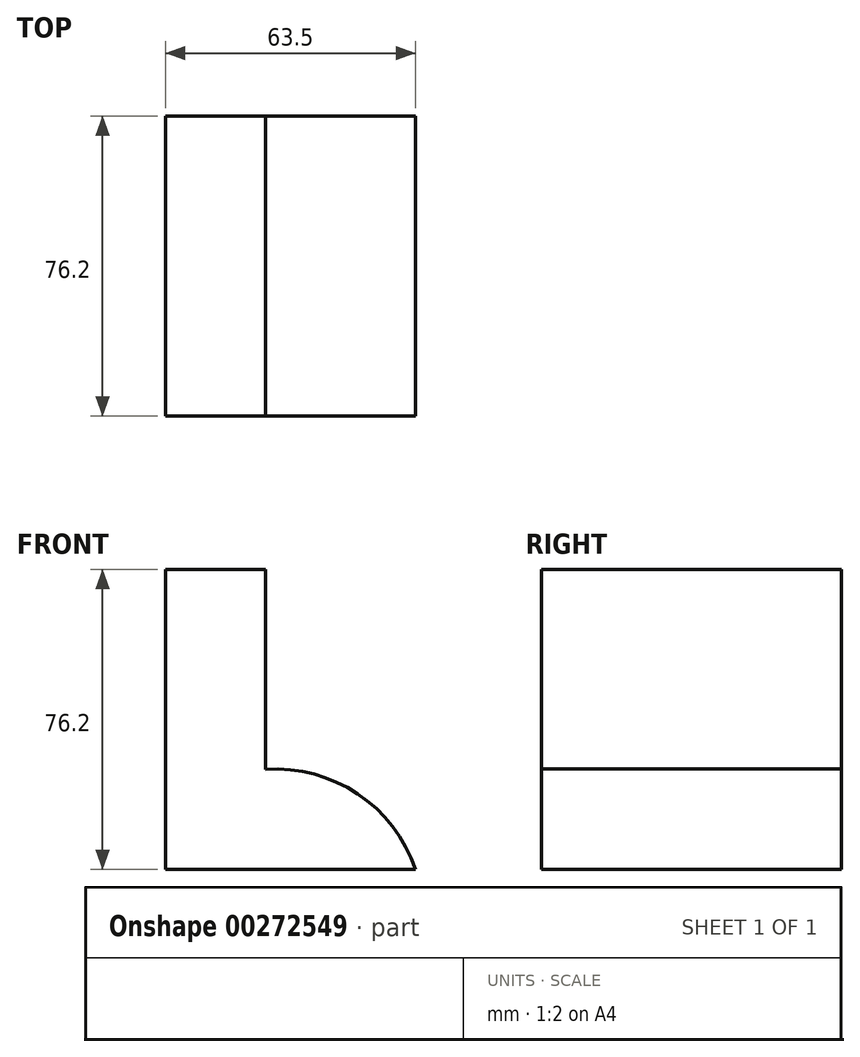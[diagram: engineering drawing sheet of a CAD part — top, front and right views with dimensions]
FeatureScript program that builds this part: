
annotation { "Feature Type Name" : "Feature", "Feature Type Description" : "" }
export const myFeature = defineFeature(function(context is Context, id is Id, definition is map)
    precondition{}
    {
        {
            var Q0;
            Q0=qCreatedBy(makeId("Front.planeOp"),FACE);
            var sketch = newSketch(context, id + "F0", { "sketchPlane" : qUnion([Q0])});
            skLineSegment(sketch, "E0", {"start": v(0, 0) * mm, "end": v(0, 76.2) * mm});
            skLineSegment(sketch, "E1", {"start": v(0, 76.2) * mm, "end": v(25.4, 76.2) * mm});
            skLineSegment(sketch, "E2", {"start": v(25.4, 76.2) * mm, "end": v(25.4, 25.4) * mm});
            skLineSegment(sketch, "E3", {"start": v(0, 0) * mm, "end": v(63.5, 0) * mm});
            skArc(sketch, "E4", {"start": v(63.5, 0) * mm, "mid": v(48.78, 19.2) * mm, "end": v(25.4, 25.4) * mm});
            skSolve(sketch);
        }
        {
            var Q0;
            Q0 = qSketchRegion(id + "F0", true);
            extrude(context, id + "F1", {"entities" : qUnion([Q0]), "depth" : 76.2 * mm});
        }
    });
